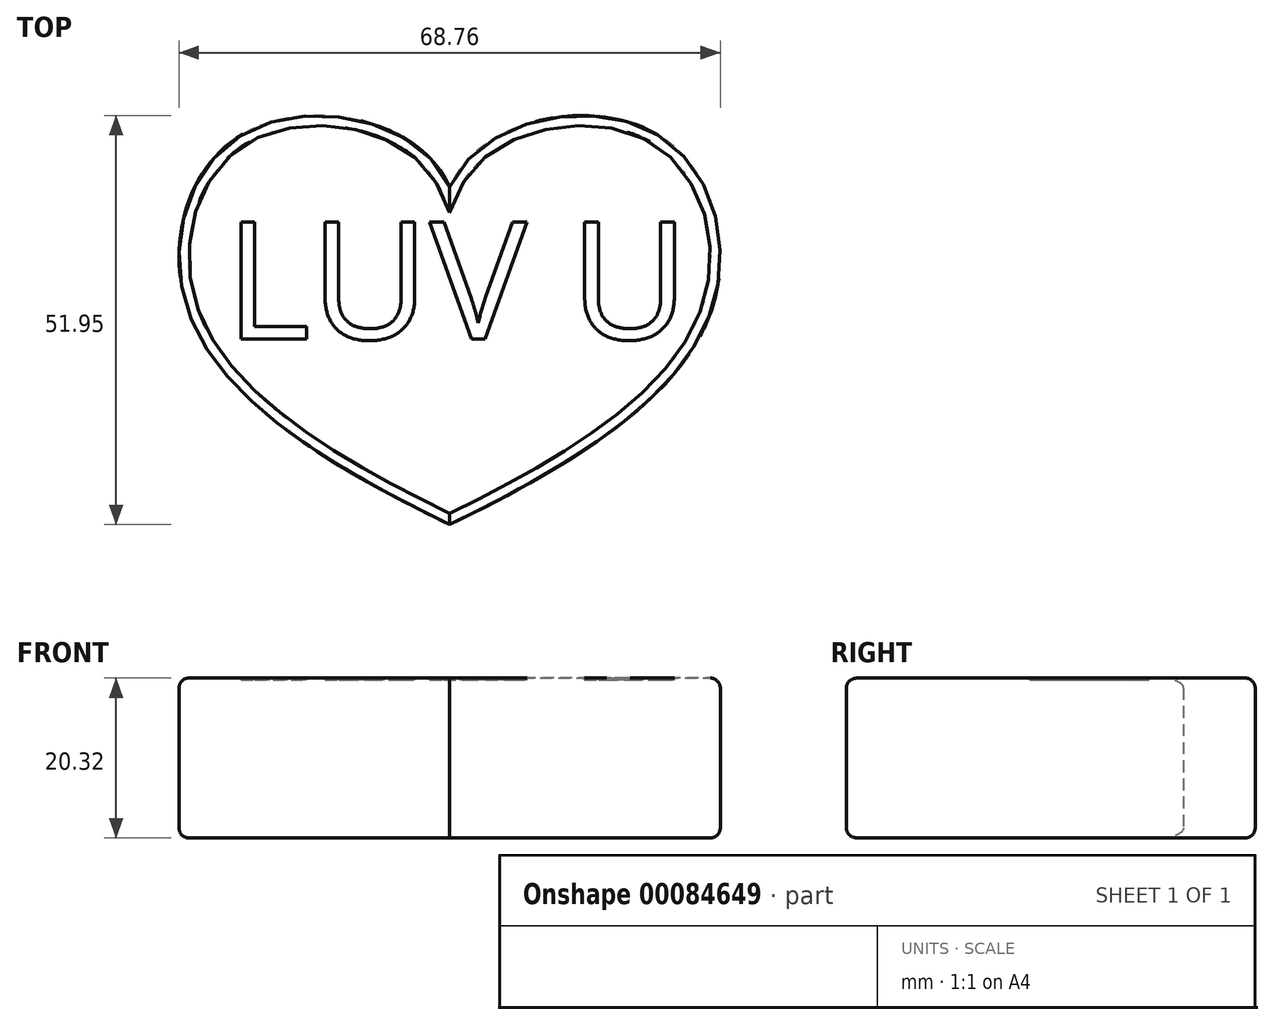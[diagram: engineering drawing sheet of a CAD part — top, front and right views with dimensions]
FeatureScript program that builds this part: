
annotation { "Feature Type Name" : "Feature", "Feature Type Description" : "" }
export const myFeature = defineFeature(function(context is Context, id is Id, definition is map)
    precondition{}
    {
        {
            var Q0;
            Q0=qCreatedBy(makeId("Top.planeOp"),FACE);
            var sketch = newSketch(context, id + "F0", { "sketchPlane" : qUnion([Q0])});
            skFitSpline(sketch, "E0", {"points": [v(0, 0) * mm, v(-25.44, 7.2) * mm, v(-33.36, -15.32) * mm, v(0, -42.85) * mm], "startDerivative": vector(-35.84, 83.42) * mm, "endDerivative": vector(118.66, -57.44) * mm});
            skLineSegment(sketch, "E1", {"start": v(0, 0) * mm, "end": v(0, -42.85) * mm});
            skSolve(sketch);
        }
        {
            var Q0;
            Q0 = qSketchRegion(id + "F0", true);
            extrude(context, id + "F1", {"entities" : qUnion([Q0]), "depth" : 20.32 * mm});
        }
        {
            var Q0;
            Q0=makeQuery(id+"F1.opExtrude","SWEPT_BODY",BODY,{"disambiguationData":[OSD([sQuery(id+"F0.wireOp",EDGE,"E0"),sQuery(id+"F0.wireOp",EDGE,"E1")])]});
            var Q1;
            Q1=qCreatedBy(makeId("Right.planeOp"),FACE);
            mirror(context, id + "F2", {"operationType" : NewBodyOperationType.ADD, "entities" : qUnion([Q0]), "mirrorPlane" : qUnion([Q1])});
        }
        {
            var Q0;
            {var subQ0=makeQuery(id+"F1.opExtrude","CAP_FACE",FACE,{"disambiguationData":[OSD([sQuery(id+"F0.wireOp",EDGE,"E0"),sQuery(id+"F0.wireOp",EDGE,"E1")])],"isStart":false});Q0=makeQuery(id+"F2.boolean.opBoolean","MERGE",FACE,{"derivedFrom":[subQ0,makeQuery(id+"F2.opPattern","COPY",FACE,{"derivedFrom":subQ0,"instanceName":"1"})]});}
            var sketch = newSketch(context, id + "F3", { "sketchPlane" : qUnion([Q0])});
            skText(sketch, "E2", { "text": "LUV U", "fontName": "OpenSans-Regular.ttf"});
            const initialGuessF3  = {"E2": [-0.02853, -0.01929, 1, 0, 0.015]};
            skSetInitialGuess(sketch, initialGuessF3);
            skSolve(sketch);
        }
        {
            var Q0;
            Q0 = qSketchRegion(id + "F3", true);
            extrude(context, id + "F4", {"entities" : qUnion([Q0]), "operationType" : NewBodyOperationType.REMOVE, "oppositeDirection" : true, "depth" : 0.25 * mm});
        }
        {
            var Q0;
            Q0=makeQuery(id+"F1.opExtrude","CAP_EDGE",EDGE,{"disambiguationData":[OSD([sQuery(id+"F0.wireOp",EDGE,"E0")])],"isStart":false});
            var Q1;
            Q1=makeQuery(id+"F2.opPattern","COPY",EDGE,{"derivedFrom":makeQuery(id+"F1.opExtrude","CAP_EDGE",EDGE,{"disambiguationData":[OSD([sQuery(id+"F0.wireOp",EDGE,"E0")])],"isStart":false}),"instanceName":"1"});
            var Q2;
            Q2=makeQuery(id+"F1.opExtrude","CAP_EDGE",EDGE,{"disambiguationData":[OSD([sQuery(id+"F0.wireOp",EDGE,"E0")])],"isStart":true});
            var Q3;
            Q3=makeQuery(id+"F2.opPattern","COPY",EDGE,{"derivedFrom":makeQuery(id+"F1.opExtrude","CAP_EDGE",EDGE,{"disambiguationData":[OSD([sQuery(id+"F0.wireOp",EDGE,"E0")])],"isStart":true}),"instanceName":"1"});
            fillet(context, id + "F5", {"entities" : qUnion([Q0, Q1, Q2, Q3]), "radius" : 1.27 * mm, "tangentPropagation" : true, "allowEdgeOverflow" : false});
        }
    });
